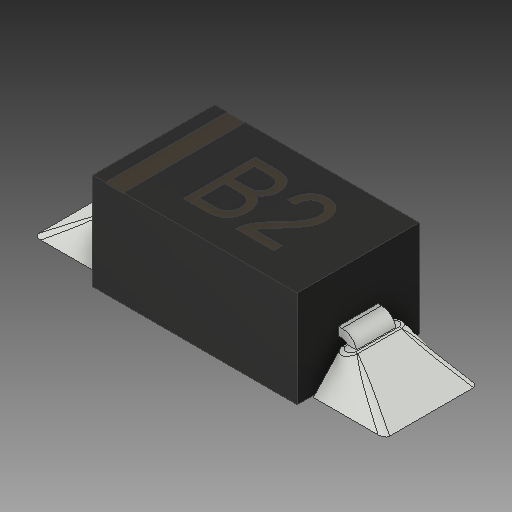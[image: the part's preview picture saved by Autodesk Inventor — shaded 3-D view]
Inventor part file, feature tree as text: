
AUTODESK INVENTOR PART (.ipt)
format: ipt  version: 2019.4 (Build 234330000, 330)  size: 337,920 bytes
history: native  units: mm
features: fillet x1
ambient origin geometry x8: Origin, YZ Plane, XZ Plane, XY Plane, X Axis, Y Axis, Z Axis, Center Point
bodies: Solid1 (feature_tree)
feature tree (1):
  fillet  "Fillet9"  [1 undecoded]
note: 1 required parameter value undecoded (feature->parameter linkage not recoverable at this tier; creation-order binding heuristic only, values carry confidence <= 0.55)
